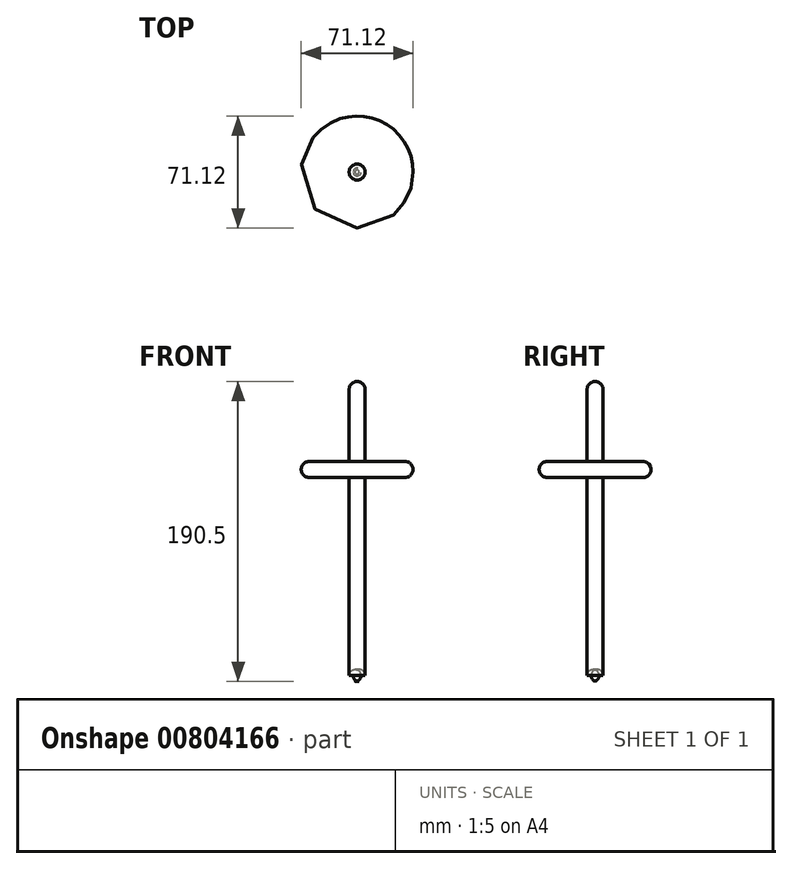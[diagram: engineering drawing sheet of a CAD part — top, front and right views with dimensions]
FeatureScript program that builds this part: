
annotation { "Feature Type Name" : "Feature", "Feature Type Description" : "" }
export const myFeature = defineFeature(function(context is Context, id is Id, definition is map)
    precondition{}
    {
        {
            var Q0;
            Q0=qCreatedBy(makeId("Top.planeOp"),FACE);
            var sketch = newSketch(context, id + "F0", { "sketchPlane" : qUnion([Q0])});
            skCircle(sketch, "E0", {"center": v(0, 0) * mm, "radius": 5.08 * mm});
            skSolve(sketch);
        }
        {
            var Q0;
            Q0 = qSketchRegion(id + "F0", true);
            extrude(context, id + "F1", {"entities" : qUnion([Q0]), "depth" : 190.5 * mm, "offsetDistance" : 25.4 * mm});
        }
        {
            var Q0;
            Q0=qCreatedBy(makeId("Top.planeOp"),FACE);
            cPlane(context, id + "F2", {"entities" : qUnion([Q0]), "cplaneType" : CPlaneType.OFFSET, "offset" : 76.2 * mm, "width" : 152.4 * mm, "height" : 152.4 * mm});
        }
        {
            var Q0;
            Q0=qCreatedBy(id+"F2.planeOp",FACE);
            cPlane(context, id + "F3", {"entities" : qUnion([Q0]), "cplaneType" : CPlaneType.OFFSET, "offset" : 25.4 * mm, "width" : 152.4 * mm, "height" : 152.4 * mm});
        }
        {
            var Q0;
            Q0=qCreatedBy(id+"F3.planeOp",FACE);
            cPlane(context, id + "F4", {"entities" : qUnion([Q0]), "cplaneType" : CPlaneType.OFFSET, "offset" : 25.4 * mm, "width" : 152.4 * mm, "height" : 152.4 * mm});
        }
        {
            var Q0;
            Q0=qCreatedBy(id+"F4.planeOp",FACE);
            cPlane(context, id + "F5", {"entities" : qUnion([Q0]), "cplaneType" : CPlaneType.OFFSET, "offset" : 25.4 * mm, "width" : 152.4 * mm, "height" : 152.4 * mm});
        }
        {
            var Q0;
            Q0=qCreatedBy(id+"F4.planeOp",FACE);
            cPlane(context, id + "F6", {"entities" : qUnion([Q0]), "cplaneType" : CPlaneType.OFFSET, "offset" : 2.54 * mm, "width" : 152.4 * mm, "height" : 152.4 * mm});
        }
        {
            var Q0;
            Q0=qCreatedBy(id+"F6.planeOp",FACE);
            var sketch = newSketch(context, id + "F7", { "sketchPlane" : qUnion([Q0])});
            skCircle(sketch, "E1", {"center": v(0, 0) * mm, "radius": 35.56 * mm});
            skSolve(sketch);
        }
        {
            var Q0;
            Q0 = qSketchRegion(id + "F7", true);
            extrude(context, id + "F8", {"entities" : qUnion([Q0]), "operationType" : NewBodyOperationType.ADD, "depth" : 10.16 * mm, "offsetDistance" : 25.4 * mm});
        }
        {
            var Q0;
            Q0=makeQuery(id+"F8.opExtrude","CAP_EDGE",EDGE,{"disambiguationData":[OSD([sQuery(id+"F7.wireOp",EDGE,"E1")])],"isStart":false});
            var Q1;
            Q1=makeQuery(id+"F8.opExtrude","CAP_EDGE",EDGE,{"disambiguationData":[OSD([sQuery(id+"F7.wireOp",EDGE,"E1")])],"isStart":true});
            fillet(context, id + "F9", {"entities" : qUnion([Q0, Q1]), "radius" : 5.08 * mm, "tangentPropagation" : true, "allowEdgeOverflow" : false});
        }
        {
            var Q0;
            Q0=qCreatedBy(id+"F2.planeOp",FACE);
            cPlane(context, id + "F10", {"entities" : qUnion([Q0]), "cplaneType" : CPlaneType.OFFSET, "offset" : 116.84 * mm, "width" : 152.4 * mm, "height" : 152.4 * mm});
        }
        {
            var Q0;
            Q0=qCreatedBy(id+"F10.planeOp",FACE);
            var sketch = newSketch(context, id + "F11", { "sketchPlane" : qUnion([Q0])});
            skCircle(sketch, "E2", {"center": v(0, 0) * mm, "radius": 7.62 * mm});
            skSolve(sketch);
        }
        {
            var Q0;
            Q0 = qSketchRegion(id + "F11", true);
            extrude(context, id + "F12", {"entities" : qUnion([Q0]), "operationType" : NewBodyOperationType.ADD, "depth" : 5.08 * mm, "offsetDistance" : 25.4 * mm});
        }
        {
            var Q0;
            Q0=makeQuery(id+"F12.opExtrude","CAP_EDGE",EDGE,{"disambiguationData":[OSD([sQuery(id+"F11.wireOp",EDGE,"E2")])],"isStart":true});
            var Q1;
            Q1=makeQuery(id+"F12.opExtrude","CAP_EDGE",EDGE,{"disambiguationData":[OSD([sQuery(id+"F11.wireOp",EDGE,"E2")])],"isStart":false});
            fillet(context, id + "F13", {"entities" : qUnion([Q0, Q1]), "radius" : 2.54 * mm, "tangentPropagation" : true, "allowEdgeOverflow" : false});
        }
        {
            var Q0;
            Q0=makeQuery(id+"F1.opExtrude","CAP_EDGE",EDGE,{"disambiguationData":[OSD([sQuery(id+"F0.wireOp",EDGE,"E0")])],"isStart":false});
            fillet(context, id + "F14", {"entities" : qUnion([Q0]), "radius" : 5.08 * mm, "tangentPropagation" : true, "allowEdgeOverflow" : false});
        }
        {
            var Q0;
            Q0=makeQuery(id+"F12.opExtrude","SWEPT_BODY",BODY,{"disambiguationData":[OSD([sQuery(id+"F11.wireOp",EDGE,"E2")])]});
            deleteBodies(context, id + "F15", {"entities" : qUnion([Q0])});
        }
        {
            var Q0;
            Q0=makeQuery(id+"F1.opExtrude","CAP_EDGE",EDGE,{"disambiguationData":[OSD([sQuery(id+"F0.wireOp",EDGE,"E0")])],"isStart":true});
            fillet(context, id + "F16", {"entities" : qUnion([Q0]), "radius" : 3.8 * mm, "tangentPropagation" : true, "allowEdgeOverflow" : false});
        }
    });
